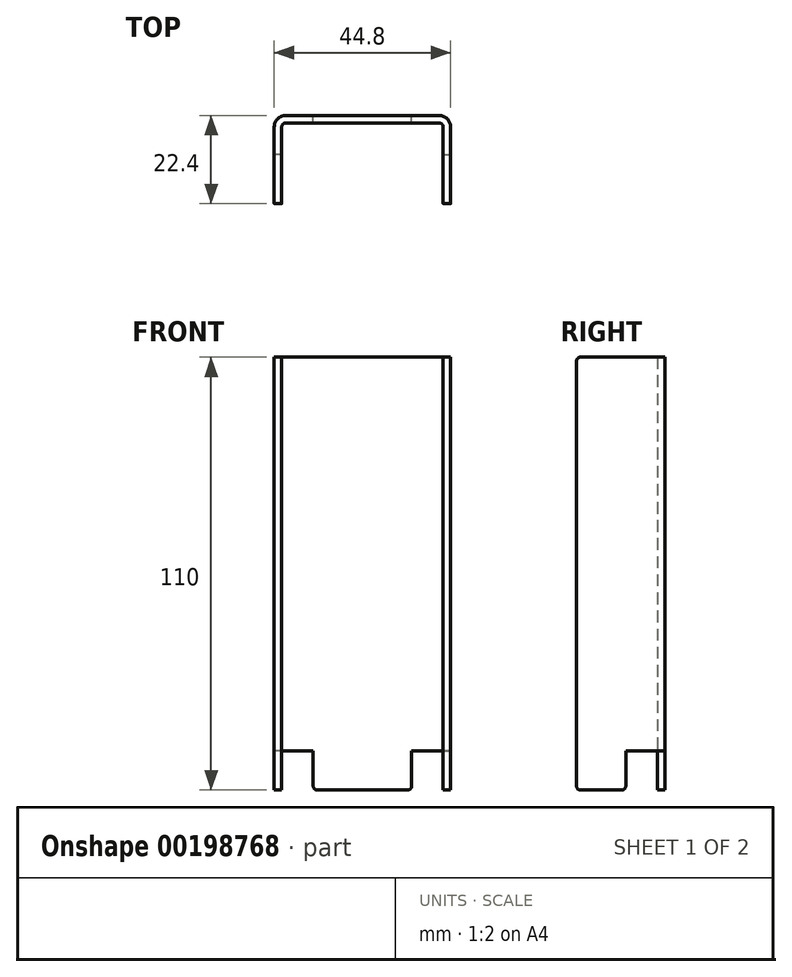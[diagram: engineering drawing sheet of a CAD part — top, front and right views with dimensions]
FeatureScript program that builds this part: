
annotation { "Feature Type Name" : "Feature", "Feature Type Description" : "" }
export const myFeature = defineFeature(function(context is Context, id is Id, definition is map)
    precondition{}
    {
        {
            var Q0;
            Q0=qCreatedBy(makeId("Top.planeOp"),FACE);
            var sketch = newSketch(context, id + "F0", { "sketchPlane" : qUnion([Q0])});
            skLineSegment(sketch, "E0.bottom", {"start": v(19.5, 10.25) * mm, "end": v(-19.5, 10.25) * mm});
            skLineSegment(sketch, "E0.left", {"start": v(20.5, 9.25) * mm, "end": v(20.5, -10.25) * mm});
            skLineSegment(sketch, "E0.right", {"start": v(-20.5, 9.25) * mm, "end": v(-20.5, -10.25) * mm});
            skPoint(sketch, "E0.middle", {"position": v(0, 0) * mm});
            skPoint(sketch, "E1.visualSharp", {"position": v(-20.5, 10.25) * mm});
            skArc(sketch, "E1.filletArc", {"start": v(-19.5, 10.25) * mm, "mid": v(-20.2, 9.96) * mm, "end": v(-20.5, 9.25) * mm});
            skPoint(sketch, "E2.visualSharp", {"position": v(20.5, 10.25) * mm});
            skArc(sketch, "E2.filletArc", {"start": v(20.5, 9.25) * mm, "mid": v(20.2, 9.96) * mm, "end": v(19.5, 10.25) * mm});
            skLineSegment(sketch, "E3.0", {"start": v(22.4, 9.25) * mm, "end": v(22.4, -10.25) * mm});
            skLineSegment(sketch, "E3.1", {"start": v(-22.4, 9.25) * mm, "end": v(-22.4, -10.25) * mm});
            skArc(sketch, "E3.2", {"start": v(-19.5, 12.15) * mm, "mid": v(-21.55, 11.3) * mm, "end": v(-22.4, 9.25) * mm});
            skLineSegment(sketch, "E3.3", {"start": v(19.5, 12.15) * mm, "end": v(-19.5, 12.15) * mm});
            skArc(sketch, "E3.4", {"start": v(22.4, 9.25) * mm, "mid": v(21.55, 11.3) * mm, "end": v(19.5, 12.15) * mm});
            skLineSegment(sketch, "E4", {"start": v(-22.4, -10.25) * mm, "end": v(-20.5, -10.25) * mm});
            skLineSegment(sketch, "E5", {"start": v(20.5, -10.25) * mm, "end": v(22.4, -10.25) * mm});
            skSolve(sketch);
        }
        {
            var Q0;
            Q0 = qSketchRegion(id + "F0", true);
            extrude(context, id + "F1", {"entities" : qUnion([Q0]), "depth" : 100 * mm, "symmetric" : true});
        }
        {
            var Q0;
            Q0=makeQuery(id+"F1.opExtrude","SWEPT_FACE",FACE,{"disambiguationData":[OSD([sQuery(id+"F0.wireOp",EDGE,"E3.3")])]});
            var sketch = newSketch(context, id + "F2", { "sketchPlane" : qUnion([Q0])});
            skLineSegment(sketch, "E6.bottom", {"start": v(12.5, -40) * mm, "end": v(-12.5, -40) * mm});
            skLineSegment(sketch, "E6.top", {"start": v(12.5, -60) * mm, "end": v(-12.5, -60) * mm});
            skLineSegment(sketch, "E6.left", {"start": v(12.5, -40) * mm, "end": v(12.5, -60) * mm});
            skLineSegment(sketch, "E6.right", {"start": v(-12.5, -40) * mm, "end": v(-12.5, -60) * mm});
            skPoint(sketch, "E6.middle", {"position": v(0, -50) * mm});
            skSolve(sketch);
        }
        {
            var Q0;
            Q0 = qSketchRegion(id + "F2", true);
            var Q1;
            Q1=makeQuery(id+"F1.opExtrude","SWEPT_FACE",FACE,{"disambiguationData":[OSD([sQuery(id+"F0.wireOp",EDGE,"E0.bottom")])]});
            extrude(context, id + "F3", {"entities" : qUnion([Q0]), "operationType" : NewBodyOperationType.ADD, "endBound" : BoundingType.UP_TO_SURFACE, "oppositeDirection" : true, "endBoundEntityFace" : qUnion([Q1]), "depth" : 25 * mm});
        }
        {
            var Q0;
            Q0=makeQuery(id+"F1.opExtrude","SWEPT_FACE",FACE,{"disambiguationData":[OSD([sQuery(id+"F0.wireOp",EDGE,"E3.0")])]});
            var sketch = newSketch(context, id + "F4", { "sketchPlane" : qUnion([Q0])});
            skLineSegment(sketch, "E7", {"start": v(-10.25, -50) * mm, "end": v(-10.25, -60) * mm});
            skLineSegment(sketch, "E8", {"start": v(-10.25, -60) * mm, "end": v(2.25, -60) * mm});
            skLineSegment(sketch, "E9", {"start": v(2.25, -60) * mm, "end": v(2.25, -50) * mm});
            skLineSegment(sketch, "E10", {"start": v(2.25, -50) * mm, "end": v(-10.25, -50) * mm});
            skSolve(sketch);
        }
        {
            var Q0;
            Q0 = qSketchRegion(id + "F4", true);
            var Q1;
            Q1=makeQuery(id+"F1.opExtrude","SWEPT_FACE",FACE,{"disambiguationData":[OSD([sQuery(id+"F0.wireOp",EDGE,"E0.left")])]});
            extrude(context, id + "F5", {"entities" : qUnion([Q0]), "endBound" : BoundingType.UP_TO_SURFACE, "oppositeDirection" : true, "endBoundEntityFace" : qUnion([Q1]), "depth" : 25 * mm});
        }
        {
            var Q0;
            Q0=makeQuery(id+"F5.opExtrude","SWEPT_BODY",BODY,{"disambiguationData":[OSD([sQuery(id+"F4.wireOp",EDGE,"E7"),sQuery(id+"F4.wireOp",EDGE,"E8"),sQuery(id+"F4.wireOp",EDGE,"E9"),sQuery(id+"F4.wireOp",EDGE,"E10")])]});
            var Q1;
            Q1=qCreatedBy(makeId("Right.planeOp"),FACE);
            mirror(context, id + "F6", {"operationType" : NewBodyOperationType.ADD, "entities" : qUnion([Q0]), "mirrorPlane" : qUnion([Q1])});
        }
        {
            var Q0;
            Q0=makeQuery(id+"F1.opExtrude","CAP_EDGE",EDGE,{"disambiguationData":[OSD([sQuery(id+"F0.wireOp",EDGE,"E5")])],"isStart":false});
            var Q1;
            Q1=makeQuery(id+"F1.opExtrude","CAP_EDGE",EDGE,{"disambiguationData":[OSD([sQuery(id+"F0.wireOp",EDGE,"E4")])],"isStart":false});
            var Q2;
            Q2=makeQuery(id+"F1.opExtrude","CAP_EDGE",EDGE,{"disambiguationData":[OSD([sQuery(id+"F0.wireOp",EDGE,"E4")])],"isStart":true});
            var Q3;
            Q3=makeQuery(id+"F1.opExtrude","CAP_EDGE",EDGE,{"disambiguationData":[OSD([sQuery(id+"F0.wireOp",EDGE,"E5")])],"isStart":true});
            var Q4;
            Q4=makeQuery(id+"F3.opExtrude","SWEPT_EDGE",EDGE,{"disambiguationData":[OSD([sQuery(id+"F2.wireOp",EDGE,"E6.top"),sQuery(id+"F2.wireOp",EDGE,"E6.right")])]});
            var Q5;
            Q5=makeQuery(id+"F3.opExtrude","SWEPT_EDGE",EDGE,{"disambiguationData":[OSD([sQuery(id+"F2.wireOp",EDGE,"E6.top"),sQuery(id+"F2.wireOp",EDGE,"E6.left")])]});
            var Q6;
            Q6=makeQuery(id+"F5.opExtrude","SWEPT_EDGE",EDGE,{"disambiguationData":[OSD([sQuery(id+"F4.wireOp",EDGE,"E8"),sQuery(id+"F4.wireOp",EDGE,"E9")])]});
            var Q7;
            Q7=makeQuery(id+"F6.opPattern","COPY",EDGE,{"derivedFrom":makeQuery(id+"F5.opExtrude","SWEPT_EDGE",EDGE,{"disambiguationData":[OSD([sQuery(id+"F4.wireOp",EDGE,"E8"),sQuery(id+"F4.wireOp",EDGE,"E9")])]}),"instanceName":"1"});
            var Q8;
            Q8=makeQuery(id+"F5.opExtrude","SWEPT_EDGE",EDGE,{"disambiguationData":[OSD([sQuery(id+"F4.wireOp",EDGE,"E7"),sQuery(id+"F4.wireOp",EDGE,"E8")])]});
            var Q9;
            Q9=makeQuery(id+"F6.opPattern","COPY",EDGE,{"derivedFrom":makeQuery(id+"F5.opExtrude","SWEPT_EDGE",EDGE,{"disambiguationData":[OSD([sQuery(id+"F4.wireOp",EDGE,"E7"),sQuery(id+"F4.wireOp",EDGE,"E8")])]}),"instanceName":"1"});
            fillet(context, id + "F7", {"entities" : qUnion([Q0, Q1, Q2, Q3, Q4, Q5, Q6, Q7, Q8, Q9]), "radius" : 1 * mm, "tangentPropagation" : true, "allowEdgeOverflow" : false});
        }
    });
